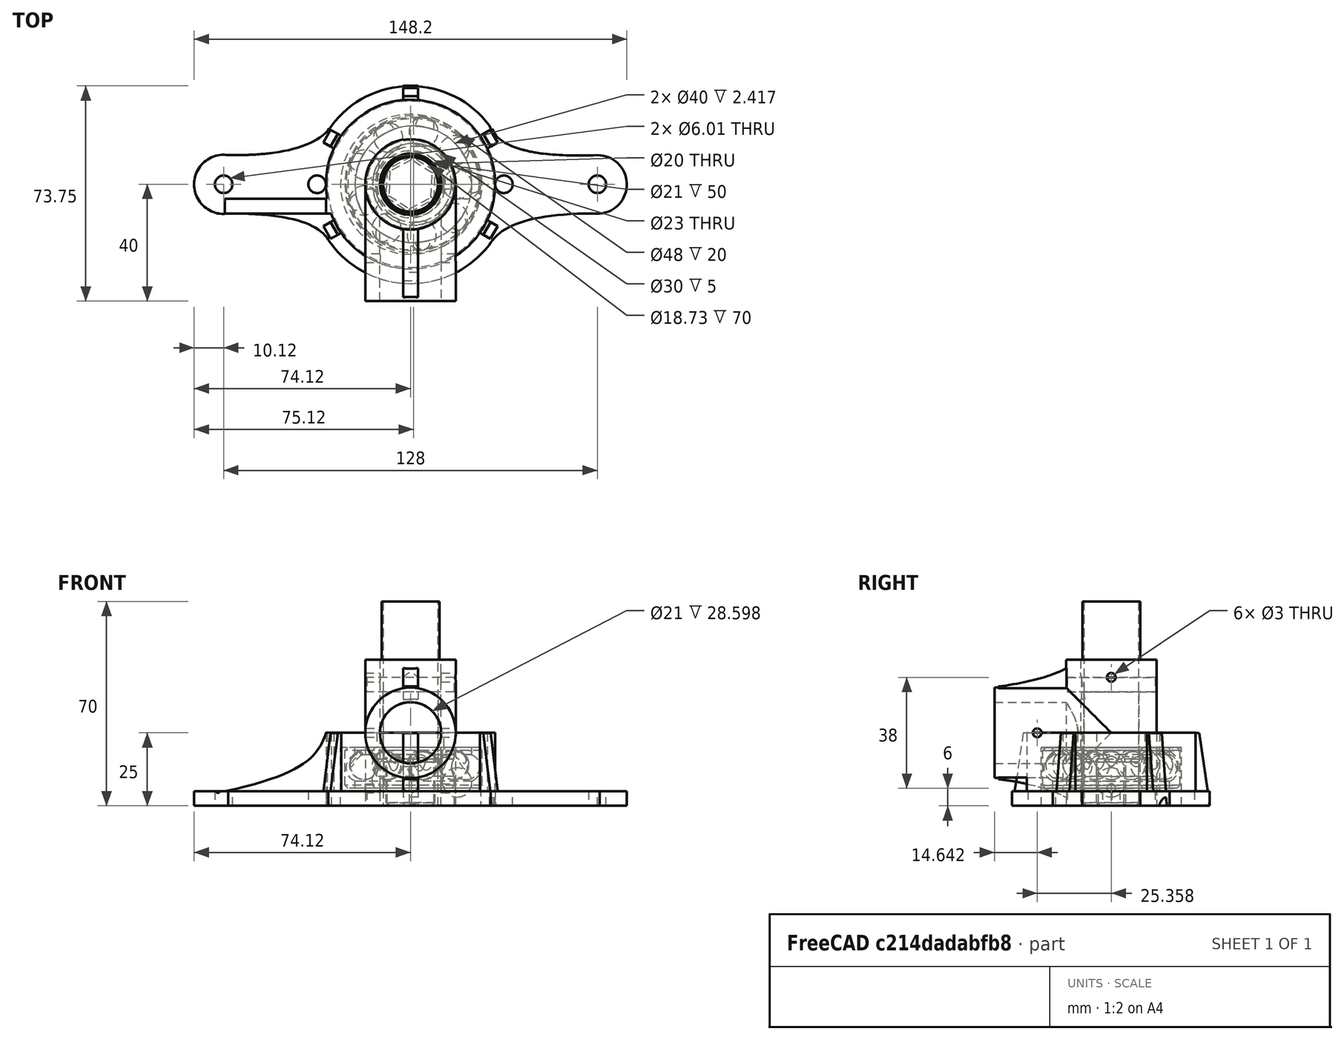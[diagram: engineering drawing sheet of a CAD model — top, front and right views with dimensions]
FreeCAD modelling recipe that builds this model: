
FCSTD DOCUMENT  (FreeCAD 1.0R39109 (Git))
Label: dressingAutomatique
License: All rights reserved
LicenseURL: http://en.wikipedia.org/wiki/All_rights_reserved
objects: Sketcher::SketchObject×16, PartDesign::Pad×10, PartDesign::Pocket×7, App::Link×6, PartDesign::Body×6, App::FeaturePython×5, Part::Chamfer×5, Part::FeaturePython×4, TechDraw::DrawViewDimension×4, TechDraw::DrawProjGroupItem×3, PartDesign::PolarPattern×2, Part::Cut×2, Assembly::JointGroup×1, PartDesign::Chamfer×1, PartDesign::LinearPattern×1, Part::Sphere×1, Part::Torus×1, PartDesign::FeatureBase×1, PartDesign::MultiTransform×1, TechDraw::DrawSVGTemplate×1, +8 more types
note: 121 computed .brp shape members not serialized (recipe doc carries the construction recipe); baked Part::Feature solids carry a one-line shape summary decoded from their .brp

FEATURE [Sketcher::SketchObject] Sketch  label="roulement"
  ArcFitTolerance = 1e-06
  AttachmentSupport = -> [XY_Plane]
  FullyConstrained = true
  MakeInternals = false
  MapMode = 5
  sketch-geometry (2):
    g0: Circle CenterX=0 CenterY=0 CenterZ=0 NormalX=0 NormalY=0 NormalZ=1 AngleXU=0 Radius=11.5
    g1: Circle CenterX=0 CenterY=0 CenterZ=0 NormalX=0 NormalY=0 NormalZ=1 AngleXU=0 Radius=29
  constraints (4):
    c: Coincident(g0,g-1)
    c: Diameter(g0) = 23
    c: Coincident(g1,g0)
    c: Diameter(g1) = 58
FEATURE [Sketcher::SketchObject] Sketch001  label="platine"
  ArcFitTolerance = 1e-06
  AttachmentSupport = -> [XY_Plane]
  FullyConstrained = false
  MakeInternals = false
  MapMode = 5
  sketch-geometry (42):
    g0: LineSegment [constr] StartX=-64.5 StartY=34 StartZ=0 EndX=-64.5 EndY=-34 EndZ=0
    g1: LineSegment [constr] StartX=-64.5 StartY=-34 StartZ=0 EndX=64.5 EndY=-34 EndZ=0
    g2: LineSegment [constr] StartX=64.5 StartY=-34 StartZ=0 EndX=64.5 EndY=34 EndZ=0
    g3: LineSegment [constr] StartX=64.5 StartY=34 StartZ=0 EndX=-64.5 EndY=34 EndZ=0
    g4: GeomPoint [constr] X=47.479 Y=17.6674 Z=0
    g5: ArcOfCircle CenterX=0 CenterY=0 CenterZ=0 NormalX=0 NormalY=0 NormalZ=1 AngleXU=0 Radius=34 StartAngle=3.73456 EndAngle=5.65431
    g6: Circle [constr] CenterX=-62.443 CenterY=-10 CenterZ=0 NormalX=0 NormalY=0 NormalZ=1 AngleXU=0 Radius=1
    g7: Circle [constr] CenterX=-33.5653 CenterY=-9.84859 CenterZ=0 NormalX=0 NormalY=0 NormalZ=1 AngleXU=0 Radius=1
    g8: Circle [constr] CenterX=-28.1957 CenterY=-19 CenterZ=0 NormalX=0 NormalY=0 NormalZ=1 AngleXU=0 Radius=1
    g9: BSplineCurve PolesCount=3 KnotsCount=2 Degree=2 IsPeriodic=0
    g10: GeomPoint [constr] X=-62.443 Y=-10 Z=0
    g11: GeomPoint [constr] X=-28.1957 Y=-19 Z=0
    g12: LineSegment [constr] StartX=-139.75 StartY=-10 StartZ=0 EndX=108.432 EndY=-10 EndZ=0
    g13: LineSegment [constr] StartX=-56.9057 StartY=-20 StartZ=0 EndX=73.6028 EndY=-20 EndZ=0
    g14: ArcOfCircle CenterX=-64 CenterY=0 CenterZ=0 NormalX=0 NormalY=0 NormalZ=1 AngleXU=0 Radius=10.1205 StartAngle=1.41634 EndAngle=4.86685
    g15: BSplineCurve PolesCount=3 KnotsCount=2 Degree=2 IsPeriodic=0
    g16: Circle [constr] CenterX=-62.443 CenterY=10 CenterZ=0 NormalX=0 NormalY=0 NormalZ=1 AngleXU=0 Radius=1
    g17: Circle [constr] CenterX=-33.9289 CenterY=9.66678 CenterZ=0 NormalX=0 NormalY=0 NormalZ=1 AngleXU=0 Radius=1
    g18: Circle [constr] CenterX=-27.0839 CenterY=20.0395 CenterZ=0 NormalX=0 NormalY=0 NormalZ=1 AngleXU=0 Radius=1
    g19: GeomPoint [constr] X=-62.443 Y=10 Z=0
    g20: GeomPoint [constr] X=-27.0839 Y=20.0395 Z=0
    g21: ArcOfCircle CenterX=0 CenterY=0 CenterZ=0 NormalX=0 NormalY=0 NormalZ=1 AngleXU=0 Radius=33.6915 StartAngle=0.637008 EndAngle=2.50458
    g22: ArcOfCircle CenterX=64.071 CenterY=-0.013204 CenterZ=0 NormalX=0 NormalY=0 NormalZ=1 AngleXU=0 Radius=10.0132 StartAngle=4.78503 EndAngle=7.85398
    g23: BSplineCurve PolesCount=3 KnotsCount=2 Degree=2 IsPeriodic=0
    g24: BSplineCurve PolesCount=3 KnotsCount=2 Degree=2 IsPeriodic=0
    g25: Circle [constr] CenterX=64.071 CenterY=10 CenterZ=0 NormalX=0 NormalY=0 NormalZ=1 AngleXU=0 Radius=1
    g26: Circle [constr] CenterX=31.305 CenterY=8.64637 CenterZ=0 NormalX=0 NormalY=0 NormalZ=1 AngleXU=0 Radius=1
    g27: Circle [constr] CenterX=27.0839 CenterY=20.0395 CenterZ=0 NormalX=0 NormalY=0 NormalZ=1 AngleXU=0 Radius=1
    g28: GeomPoint [constr] X=64.071 Y=10 Z=0
    g29: GeomPoint [constr] X=27.0839 Y=20.0395 Z=0
    g30: Circle [constr] CenterX=64.7978 CenterY=-10 CenterZ=0 NormalX=0 NormalY=0 NormalZ=1 AngleXU=0 Radius=1
    g31: Circle [constr] CenterX=33.9289 CenterY=-9.66678 CenterZ=0 NormalX=0 NormalY=0 NormalZ=1 AngleXU=0 Radius=1
    g32: Circle [constr] CenterX=27.4955 CenterY=-20 CenterZ=0 NormalX=0 NormalY=0 NormalZ=1 AngleXU=0 Radius=1
    g33: GeomPoint [constr] X=64.7978 Y=-10 Z=0
    g34: GeomPoint [constr] X=27.4955 Y=-20 Z=0
    g35: LineSegment [constr] StartX=-146.84 StartY=10 StartZ=0 EndX=88.6661 EndY=10 EndZ=0
    g36: LineSegment [constr] StartX=-56.9057 StartY=20.0395 StartZ=0 EndX=73.6028 EndY=20.0395 EndZ=0
    g37: Circle CenterX=-32 CenterY=0 CenterZ=0 NormalX=0 NormalY=0 NormalZ=1 AngleXU=0 Radius=3.00257
    g38: Circle CenterX=0 CenterY=0 CenterZ=0 NormalX=0 NormalY=0 NormalZ=1 AngleXU=0 Radius=3.00257
    g39: Circle CenterX=32 CenterY=0 CenterZ=0 NormalX=0 NormalY=0 NormalZ=1 AngleXU=0 Radius=3.00257
    g40: Circle CenterX=-64 CenterY=0 CenterZ=0 NormalX=0 NormalY=0 NormalZ=1 AngleXU=0 Radius=3.005
    g41: Circle CenterX=64 CenterY=0 CenterZ=0 NormalX=0 NormalY=0 NormalZ=1 AngleXU=0 Radius=3.00257
  constraints (71):
    c: Coincident(g0,g1)
    c: Coincident(g1,g2)
    c: Coincident(g2,g3)
    c: Coincident(g3,g0)
    c: Vertical(g0)
    c: Horizontal(g1)
    c: DistanceY(g2,g2) = 68
    c: DistanceX(g1,g1) = 129
    c: Symmetric(g2,g1,g-1)
    c: Symmetric(g2,g0,g-2)
    c: Weight(g6) = 1
    c: Equal(g6,g7)
    c: Equal(g6,g8)
    c: InternalAlignment(g6,g9)
    c: InternalAlignment(g7,g9)
    c: InternalAlignment(g8,g9)
    c: InternalAlignment(g10,g9)
    c: InternalAlignment(g11,g9)
    c: Coincident(g8,g5)
    c: Horizontal(g12)
    c: Distance(g12,g-1) = 10
    c: Horizontal(g13)
    c: Tangent(g13,g8)
    c: Distance(g13,g-1) = 20
    c: PointOnObject(g5,g13)
    c: Tangent(g5,g1)
    c: Weight(g16) = 1
    c: Equal(g16,g17)
    c: Equal(g16,g18)
    c: InternalAlignment(g16-g20 -> g15) x5
    c: Coincident(g16,g14)
    c: Coincident(g21,g15)
    c: Coincident(g14,g9)
    c: Weight(g30) = 1
    c: Equal(g30,g31)
    c: Equal(g30,g32)
    c: InternalAlignment(g30-g34 -> g24) x5
    c: Weight(g25) = 1
    c: Equal(g25,g26)
    c: Equal(g25,g27)
    c: InternalAlignment(g25-g29 -> g23) x5
    c: Coincident(g25,g22)
    c: Coincident(g22,g24)
    c: Coincident(g24,g5)
    c: Coincident(g23,g21)
    c: PointOnObject(g14,g-1)
    c: PointOnObject(g22,g12)
    c: Horizontal(g35)
    c: Horizontal(g36)
    c: PointOnObject(g21,g36)
    c: PointOnObject(g15,g36)
    c: Diameter(g37) = 6.00515
    c: Diameter(g38) = 6.00515
    c: Diameter(g39) = 6.00515
    c: Coincident(g-1,g5)
    c: Coincident(g-1,g21)
    c: Coincident(g38,g5)
    c: PointOnObject(g37,g-1)
    c: PointOnObject(g39,g-1)
    c: DistanceX(g37,g5) = 32
    c: DistanceX(g5,g39) = 32
    c: PointOnObject(g23,g35)
    c: Diameter(g40) = 6.01
    c: DistanceX(g40,g37) = 32
    c: PointOnObject(g15,g35)
    c: PointOnObject(g9,g12)
    c: Diameter(g41) = 6.00515
    c: PointOnObject(g41,g-1)
    c: DistanceX(g39,g41) = 32
    c: Coincident(g14,g40)
    c: Distance(g35,g-1) = 10
FEATURE [Sketcher::SketchObject] Sketch003  label="renfprt"
  ArcFitTolerance = 1e-06
  AttachmentOffset = pos=(30,0,0) rot=(0,0,1;0rad)
  AttachmentSupport = -> [YZ_Plane]
  FullyConstrained = false
  MakeInternals = false
  MapMode = 5
  Placement = pos=(0,30,0) rot=(0.57735,0.57735,0.57735;2.0944rad)
  sketch-geometry (4):
    g0: LineSegment StartX=-2.07385 StartY=24.959 StartZ=0 EndX=-2.07385 EndY=0 EndZ=0
    g1: LineSegment StartX=-2.07385 StartY=0 StartZ=0 EndX=3.74646 EndY=0 EndZ=0
    g2: LineSegment StartX=-2.07385 StartY=24.959 StartZ=0 EndX=0.193659 EndY=24.959 EndZ=0
    g3: LineSegment StartX=0.193659 StartY=24.959 StartZ=0 EndX=3.74646 EndY=0 EndZ=0
  constraints (8):
    c: Coincident(g0,g1)
    c: Vertical(g0)
    c: Horizontal(g1)
    c: PointOnObject(g1,g-1)
    c: Coincident(g2,g0)
    c: Coincident(g3,g2)
    c: Coincident(g3,g1)
    c: Horizontal(g2)
FEATURE [Sketcher::SketchObject] Sketch004  label="axe"
  ArcFitTolerance = 1e-06
  AttachmentSupport = -> [XY_Plane001]
  FullyConstrained = true
  MakeInternals = false
  MapMode = 5
  sketch-geometry (2):
    g0: Circle CenterX=0 CenterY=0 CenterZ=0 NormalX=0 NormalY=0 NormalZ=1 AngleXU=0 Radius=15
    g1: Circle CenterX=0 CenterY=0 CenterZ=0 NormalX=0 NormalY=0 NormalZ=1 AngleXU=0 Radius=9.5
  constraints (4):
    c: Coincident(g0,g-1)
    c: Diameter(g0) = 30
    c: Coincident(g1,g0)
    c: Diameter(g1) = 19
FEATURE [PartDesign::Pad] Pad004  label="bute axe"
  Direction = (0,0,1)
  Length = 44
  Length2 = 10
  Profile = -> Sketch004 [Edge1]
  ReferenceAxis = -> Sketch004 [N_Axis]
  Suppressed = false
  Type = 0
FEATURE [PartDesign::Pocket] Pocket001  label="axe001"
  BaseFeature = -> Pad004
  Direction = (0,0,-1)
  Length = 39
  Length2 = 5
  Profile = -> Sketch004
  ReferenceAxis = -> Sketch004 [N_Axis]
  Reversed = true
  Suppressed = false
  Type = 0
FEATURE [Sketcher::SketchObject] Sketch005  label="hexa"
  ArcFitTolerance = 1e-06
  AttachmentSupport = -> [XY_Plane001]
  ExternalGeometry = -> [Sketch004]
  FullyConstrained = false
  MakeInternals = false
  MapMode = 5
  sketch-geometry (8):
    g0: LineSegment StartX=8.03876 StartY=-5.06244 StartZ=0 EndX=8.40359 EndY=4.43055 EndZ=0
    g1: LineSegment StartX=8.40359 StartY=4.43055 StartZ=0 EndX=0.364825 EndY=9.49299 EndZ=0
    g2: LineSegment StartX=0.364825 StartY=9.49299 StartZ=0 EndX=-8.03876 EndY=5.06244 EndZ=0
    g3: LineSegment StartX=-8.03876 StartY=5.06244 StartZ=0 EndX=-8.40359 EndY=-4.43055 EndZ=0
    g4: LineSegment StartX=-8.40359 StartY=-4.43055 StartZ=0 EndX=-0.364825 EndY=-9.49299 EndZ=0
    g5: LineSegment StartX=-0.364825 StartY=-9.49299 StartZ=0 EndX=8.03876 EndY=-5.06244 EndZ=0
    g6: Circle [constr] CenterX=0 CenterY=0 CenterZ=0 NormalX=0 NormalY=0 NormalZ=1 AngleXU=0 Radius=9.5
    g7: Circle CenterX=0 CenterY=0 CenterZ=0 NormalX=0 NormalY=0 NormalZ=1 AngleXU=0 Radius=12.1402
  constraints (16):
    c: Coincident(g0,g1)
    c: Coincident(g1,g2)
    c: Coincident(g2,g3)
    c: Coincident(g3,g4)
    c: Coincident(g4,g5)
    c: Coincident(g5,g0)
    c: Equal(g0, g1-g5) x5
    c: PointOnObject(g0,g6)
    c: PointOnObject(g1,g6)
    c: PointOnObject(g2,g6)
    c: PointOnObject(g3,g6)
    c: PointOnObject(g4,g6)
    c: PointOnObject(g5,g6)
    c: Coincident(g6,g-1)
    c: PointOnObject(g5,g-3)
    c: Coincident(g7,g6)
FEATURE [PartDesign::Pocket] Pocket002
  BaseFeature = -> Pocket001
  Direction = (0,0,-1)
  Length = 15
  Length2 = 5
  Profile = -> Sketch005
  ReferenceAxis = -> Sketch005 [N_Axis]
  Reversed = true
  Suppressed = false
  Type = 0
FEATURE [App::Link] Support_mur  label="Support mur001"
  LinkedObject = -> Body
FEATURE [App::FeaturePython] GroundedJoint  # Assembly grounded joint (typed FeaturePython)
  ObjectToGround = -> Support_mur
FEATURE [Assembly::JointGroup] Joints
  Group = -> [GroundedJoint]
FEATURE [App::Link] Axe  label="Axe001"
  LinkPlacement = pos=(-8.9e-15,-2.04251e-06,32) rot=(1,0,0;3.14159rad)
  LinkedObject = -> Body001
  Placement = pos=(-8.9e-15,-2.04251e-06,32) rot=(1,0,0;3.14159rad)
FEATURE [PartDesign::Chamfer] Chamfer
  Angle = 45
  Base = -> Pocket002 [Edge25,Edge23,Edge21,Edge30,Face17,Edge27]
  BaseFeature = -> Pocket002
  ChamferType = 0
  FlipDirection = false
  Size = 1
  Size2 = 1
  SupportTransform = false
  Suppressed = false
  UseAllEdges = false
FEATURE [PartDesign::Body] Body001  label="Axe"
  AllowCompound = false
  Group = -> [Sketch004,Pad004,Pocket001,Sketch005,Pocket002,Chamfer]
  Origin = -> Origin001
  Tip = -> Chamfer
FEATURE [Sketcher::SketchObject] Sketch006
  ArcFitTolerance = 1e-06
  AttachmentOffset = pos=(0,0,5) rot=(0,0,1;0rad)
  AttachmentSupport = -> [XZ_Plane]
  FullyConstrained = false
  MakeInternals = false
  MapMode = 5
  Placement = pos=(0,-5,1.1e-15) rot=(1,0,0;1.5708rad)
  sketch-geometry (11):
    g0: LineSegment StartX=-66.3753 StartY=4.44189 StartZ=0 EndX=-26.6331 EndY=4.44189 EndZ=0
    g1: LineSegment StartX=-26.6331 StartY=4.44189 StartZ=0 EndX=-26.6331 EndY=25 EndZ=0
    g2: GeomPoint [constr] X=-28.9519 Y=25 Z=0
    g3: GeomPoint [constr] X=-38.0241 Y=13.5983 Z=0
    g4: GeomPoint [constr] X=-66.3753 Y=4.44189 Z=0
    g5: BSplineCurve PolesCount=4 KnotsCount=2 Degree=3 IsPeriodic=0
    g6-g9: Circle [constr] x4 (B-spline internal-alignment scaffolding for g5; pole/knot coordinates omitted)
    g10: LineSegment StartX=-26.6331 StartY=25 StartZ=0 EndX=-28.9519 EndY=25 EndZ=0
  constraints (19):
    c: Vertical(g1)
    c: InternalAlignment(g2,g5)
    c: PointOnObject(g3,g5)
    c: InternalAlignment(g4,g5)
    c: InternalAlignment(g6,g5)
    c: Weight(g6) = 1
    c: InternalAlignment(g7,g5)
    c: Equal(g7,g6)
    c: InternalAlignment(g8,g5)
    c: Equal(g8,g6)
    c: InternalAlignment(g9,g5)
    c: Equal(g9,g6)
    c: Coincident(g1,g0)
    c: Coincident(g5,g0)
    c: Horizontal(g0)
    c: PointOnObject(g1,g-3)
    c: Coincident(g10,g1)
    c: PointOnObject(g10,g-3)
    c: Coincident(g5,g10)
FEATURE [PartDesign::LinearPattern] LinearPattern
  Direction = -> Y_Axis
  Length = 15
  Mode = 0
  Occurrences = 2
  Offset = 15
  Suppressed = false
  TransformMode = 0
FEATURE [PartDesign::PolarPattern] PolarPattern002
  Angle = 360
  Axis = -> Z_Axis
  Mode = 0
  Occurrences = 2
  Offset = 120
  Suppressed = false
  TransformMode = 0
FEATURE [Part::Sphere] Sphere
  Angle1 = -90
  Angle2 = 90
  Angle3 = 360
  AttacherType = Attacher::AttachEngine3D
  Placement = pos=(16,0,8) rot=(0,0,1;0rad)
  Radius = 5
FEATURE [Part::FeaturePython] Tube  # WARN: FeaturePython — macro-defined, semantics opaque (R4)
  AttacherType = Attacher::AttachEngine3D
  Height = 14
  InnerRadius = 10
  OuterRadius = 14
FEATURE [Part::Torus] Torus
  Angle1 = -180
  Angle2 = 180
  Angle3 = 360
  AttacherType = Attacher::AttachEngine3D
  Placement = pos=(0,0,7) rot=(0,0,1;0rad)
  Radius1 = 18
  Radius2 = 5
FEATURE [Part::FeaturePython] Tube001  # WARN: FeaturePython — macro-defined, semantics opaque (R4)
  AttacherType = Attacher::AttachEngine3D
  Height = 14
  InnerRadius = 20
  OuterRadius = 23.5
FEATURE [Part::Cut] Cut002
  Base = -> Tube001
  Tool = -> Torus
FEATURE [Part::Cut] Cut
  Base = -> Tube
  Tool = -> Torus
FEATURE [Part::Chamfer] Chamfer001
  Base = -> Cut002
  EdgeLinks = -> Cut002 [Edge1]
  Edges = 1 edges r=1: [Edge1]
FEATURE [Part::Chamfer] Chamfer002
  Base = -> Chamfer001
  EdgeLinks = -> Chamfer001 [Edge3]
  Edges = 1 edges r=1: [Edge3]
FEATURE [Part::Chamfer] Chamfer003
  Base = -> Cut
  EdgeLinks = -> Cut [Edge3]
  Edges = 1 edges r=1: [Edge3]
FEATURE [Part::Chamfer] Chamfer004
  Base = -> Chamfer003
  EdgeLinks = -> Chamfer003 [Edge8]
  Edges = 1 edges r=1: [Edge8]
FEATURE [Part::Chamfer] Chamfer005
  Base = -> Chamfer004
  EdgeLinks = -> Chamfer004 [Edge8,Edge11]
  Edges = 2 edges r=1: [Edge8,Edge11]
FEATURE [Part::FeaturePython] Array  # Draft array (typed FeaturePython)
  AlwaysSyncPlacement = false
  Angle = 360
  ArrayType = 1
  Axis = (0,0,1)
  Base = -> Sphere
  Center = (-1.96,0.32,0.26)
  Count = 9
  ExpandArray = false
  Fuse = false
  IntervalAxis = (0,0,0)
  IntervalX = (50,0,0)
  IntervalY = (0,50,0)
  IntervalZ = (0,0,50)
  NumberCircles = 3
  NumberPolar = 9
  NumberX = 2
  NumberY = 2
  NumberZ = 1
  Placement = pos=(2,-2.38419e-07,0) rot=(0,0,1;0rad)
  PlacementList = 9 placements: [(16,0,8),(12.0039,11.6193,8),(1.47386,17.9516,8),(-10.6629,16.0338,8),(-18.7274,6.76338,8),(-18.9463,-5.52198,8),(-11.2171,-15.0738,8),(0.843583,-17.4227,8),(11.5925,-11.4696,8)]
  RadialDistance = 50
  ScaleList = (9) [(1,1,1),(1,1,1),(1,1,1),(1,1,1),(1,1,1),(1,1,1),(1,1,1),(1,1,1),(1,1,1)]
  Symmetry = 1
  TangentialDistance = 25
FEATURE [Part::FeaturePython] Connect  # WARN: FeaturePython — macro-defined, semantics opaque (R4)
  Objects = -> [Chamfer002,Chamfer005,Array]
  Tolerance = 0
FEATURE [PartDesign::FeatureBase] BaseFeature
  BaseFeature = -> Connect
  Suppressed = false
FEATURE [PartDesign::Body] Body002  label="Roulement"
  AllowCompound = false
  BaseFeature = -> Connect
  Group = -> [BaseFeature]
  Origin = -> Origin003
  Placement = pos=(0.999972,4.76837e-06,6.00003) rot=(0,0,1;0rad)
  Tip = -> BaseFeature
FEATURE [Sketcher::SketchObject] Sketch007  label="roulement insert"
  ArcFitTolerance = 1e-06
  AttachmentSupport = -> [XY_Plane]
  FullyConstrained = true
  MakeInternals = false
  MapMode = 5
  sketch-geometry (1):
    g0: Circle CenterX=0 CenterY=0 CenterZ=0 NormalX=0 NormalY=0 NormalZ=1 AngleXU=0 Radius=24
  constraints (2):
    c: Coincident(g0,g-1)
    c: Radius(g0) = 24
FEATURE [PartDesign::Pad] Pad
  Direction = (0,0,1)
  Length = 25
  Length2 = 10
  Profile = -> Sketch
  ReferenceAxis = -> Sketch [N_Axis]
  Suppressed = false
  Type = 0
FEATURE [PartDesign::Pad] Pad001
  BaseFeature = -> Pad
  Direction = (0,0,1)
  Length = 5
  Length2 = 10
  Profile = -> Sketch001
  ReferenceAxis = -> Sketch001 [N_Axis]
  Suppressed = false
  Type = 0
FEATURE [PartDesign::Pocket] Pocket
  BaseFeature = -> Pad001
  Direction = (0,0,-1)
  Length = 20
  Length2 = 10
  Profile = -> Sketch007
  ReferenceAxis = -> Sketch007 [N_Axis]
  Reversed = true
  Suppressed = false
  Type = 4
FEATURE [PartDesign::Pad] Pad003  label="renfort roulement"
  BaseFeature = -> Pocket
  Direction = (1,0,0)
  Length = 2.5
  Length2 = 2.5
  Profile = -> Sketch003
  ReferenceAxis = -> Sketch003 [N_Axis]
  Suppressed = false
  Type = 4
FEATURE [PartDesign::PolarPattern] PolarPattern
  Angle = 360
  Axis = -> Z_Axis
  BaseFeature = -> Pad003
  Mode = 0
  Occurrences = 6
  Offset = 120
  Originals = -> [Pad003]
  Suppressed = false
  TransformMode = 0
FEATURE [PartDesign::Pad] Pad005  label="renfort platine"
  BaseFeature = -> PolarPattern
  Direction = (0,-1,2e-16)
  Length = 5
  Length2 = 15
  Profile = -> Sketch006
  ReferenceAxis = -> Sketch006 [N_Axis]
  Suppressed = false
  Type = 0
FEATURE [PartDesign::MultiTransform] MultiTransform
  BaseFeature = -> Pad005
  Originals = -> [Pad005]
  Suppressed = false
  TransformMode = 0
  Transformations = -> [LinearPattern,PolarPattern002]
FEATURE [Sketcher::SketchObject] Sketch008
  ArcFitTolerance = 1e-06
  AttachmentOffset = pos=(0,0,5) rot=(0,0,1;0rad)
  AttachmentSupport = -> [XY_Plane]
  ExternalGeometry = -> [Sketch001]
  FullyConstrained = true
  MakeInternals = false
  MapMode = 5
  Placement = pos=(0,0,5) rot=(0,0,1;0rad)
  sketch-geometry (2):
    g0: Circle CenterX=-32 CenterY=0 CenterZ=0 NormalX=0 NormalY=0 NormalZ=1 AngleXU=0 Radius=4.5
    g1: Circle CenterX=32 CenterY=0 CenterZ=0 NormalX=0 NormalY=0 NormalZ=1 AngleXU=0 Radius=4.5
  constraints (4):
    c: Coincident(g0,g-3)
    c: Coincident(g1,g-4)
    c: Diameter(g0) = 9
    c: Diameter(g1) = 9
FEATURE [PartDesign::Pocket] Pocket003
  BaseFeature = -> MultiTransform
  Direction = (0,0,-1)
  Length = 28
  Length2 = 5
  Profile = -> Sketch008
  ReferenceAxis = -> Sketch008 [N_Axis]
  Reversed = true
  Suppressed = false
  Type = 0
FEATURE [PartDesign::Body] Body  label="Support mur"
  AllowCompound = false
  Group = -> [Pad,Pad001,Sketch,Pocket,Sketch001,Sketch003,Pad003,PolarPattern,Sketch006,Pad005,PolarPattern002,Sketch007,Sketch008,MultiTransform,Pocket003,LinearPattern]
  Origin = -> Origin
  Tip = -> Pad005
FEATURE [TechDraw::DrawSVGTemplate] Template
  EditableTexts = approval_person=B. Hecate; creator=A. Nemesis; date_of_issue=26/01/2025; document_status=In preparation; document_type=Assembly Drawing; drawing_number=DN; general_tolerances=ISO 2768-m; language_code=EN; part_material=Stainless steel Mat.No. 1.4301; responsible_department=RD; revision_index=AAA; sheet_number=1 / 1; sheet_scale=1 : 1; supplementary_title_1=ST1; supplementary_title_2=ST2; title=dressingAutomatique
  Height = 594
  Orientation = 1
  Template = D:/Program Files/FreeCAD 1.0/data/Mod/TechDraw/Templates/A1_Landscape_ISO5457_advanced.svg
  Width = 841
FEATURE [TechDraw::DrawProjGroupItem] View  label="Front"
  CoarseView = false
  Direction = (0,-1,0)
  Focus = 100
  HardHidden = false
  IsoCount = 0
  IsoHidden = false
  IsoVisible = false
  LockPosition = true
  Perspective = false
  Rotation = 0
  RotationVector = (1,0,0)
  ScaleType = 2
  ScrubCount = 1
  SeamHidden = false
  SeamVisible = false
  SmoothHidden = false
  SmoothVisible = true
  Source = -> [Pocket003]
  Type = 0
  X = 0
  XDirection = (1,0,0)
  Y = 0
FEATURE [TechDraw::DrawProjGroupItem] ProjItem  label="Bottom"
  CoarseView = false
  Direction = (0,0,-1)
  Focus = 100
  HardHidden = false
  IsoCount = 0
  IsoHidden = false
  IsoVisible = false
  LockPosition = false
  Perspective = false
  Rotation = 0
  RotationVector = (1,0,0)
  ScaleType = 0
  ScrubCount = 1
  SeamHidden = false
  SeamVisible = false
  SmoothHidden = false
  SmoothVisible = true
  Source = -> [Pocket003]
  Type = 5
  X = 0
  XDirection = (1,0,0)
  Y = 61.3732
FEATURE [TechDraw::DrawProjGroupItem] ProjItem002  label="Top"
  CoarseView = false
  Direction = (0,0,1)
  Focus = 100
  HardHidden = false
  IsoCount = 0
  IsoHidden = false
  IsoVisible = false
  LockPosition = false
  Perspective = false
  Rotation = 0
  RotationVector = (1,0,0)
  ScaleType = 0
  ScrubCount = 1
  SeamHidden = false
  SeamVisible = false
  SmoothHidden = false
  SmoothVisible = true
  Source = -> [Pocket003]
  Type = 4
  X = 0
  XDirection = (1,0,0)
  Y = -61.3732
FEATURE [TechDraw::DrawProjGroup] ProjGroup
  Anchor = -> View
  AutoDistribute = true
  LockPosition = false
  ProjectionType = 0
  Rotation = 0
  ScaleType = 0
  Source = -> [Pocket003]
  Views = -> [View,ProjItem,ProjItem002]
  X = 225.734
  Y = 323.245
  spacingX = 15
  spacingY = 15
FEATURE [TechDraw::DrawViewBalloon] Balloon
  BubbleShape = 0
  EndType = 0
  EndTypeScale = 1
  KinkLength = 5
  LockPosition = false
  OriginX = 5.51711
  OriginY = 71.03
  Rotation = 0
  ScaleType = 0
  ShapeScale = 1
  SourceView = -> View
  Text = 1
  TextWrapLen = -1
  X = 25.5171
  Y = 91.03
FEATURE [TechDraw::DrawViewDimension] Dimension
  AngleOverride = false
  Arbitrary = false
  ArbitraryTolerances = false
  BoxCorners = (2) [(-74.1024,-33.8732,-1e-07),(74.1024,33.8732,1e-07)]
  EqualTolerance = true
  ExtensionAngle = 0
  FormatSpec = ⌀%.2w
  FormatSpecOverTolerance = %+.2w
  FormatSpecUnderTolerance = %+.2w
  Inverted = false
  LineAngle = 0
  LockPosition = false
  MeasureType = 1
  OverTolerance = 0
  References2D = -> [ProjItem]
  Rotation = 0
  ScaleType = 0
  TheoreticalExact = false
  Type = 5
  UnderTolerance = 0
  X = 67.3072
  Y = 46.6106
FEATURE [TechDraw::DrawViewSection] SectionView  label="Section  - "
  BaseView = -> View
  CoarseView = false
  CutSurfaceDisplay = 2
  Direction = (-1,0,-1e-16)
  FileGeomPattern = <path>\data\Mod/TechDraw/PAT/FCPAT.pat
  FileHatchPattern = <path>\data\Mod/TechDraw/Patterns/simple.svg
  Focus = 100
  FuseBeforeCut = false
  HardHidden = false
  HatchOffset = (0,0,0)
  HatchRotation = 0
  HatchScale = 1
  IsoCount = 0
  IsoHidden = false
  IsoVisible = false
  LockPosition = false
  NameGeomPattern = Diamond
  Perspective = false
  Rotation = -90
  ScaleType = 0
  ScrubCount = 1
  SeamHidden = false
  SeamVisible = false
  SectionDirection = 4
  SectionLineStretch = 1
  SectionNormal = (-1,0,-1e-16)
  SectionOrigin = (-0.018,-0.13,12.5)
  SmoothHidden = false
  SmoothVisible = true
  Source = -> [Pocket003]
  TrimAfterCut = false
  UsePreviousCut = false
  X = 361.548
  XDirection = (1e-16,0,-1)
  Y = 500.685
FEATURE [TechDraw::DrawViewImage] ActiveView
  Height = 102.4
  ImageFile = <userpath>/AppData/Local/cache/FreeCAD/Cache/FreeCAD_Doc_1c473428-2d88-4942-b3bc-02458ee26885_3d8759_5548/PagC9F4.tmp.png
  LockPosition = false
  Rotation = 0
  ScaleType = 2
  Width = 128
  X = 634.849
  Y = 481.794
FEATURE [TechDraw::DrawViewDimension] Dimension001
  AngleOverride = false
  Arbitrary = false
  ArbitraryTolerances = false
  BoxCorners = (2) [(-74.1024,-33.8732,-1e-07),(74.1024,33.8732,1e-07)]
  EqualTolerance = true
  ExtensionAngle = 0
  FormatSpec = ⌀%.2w
  FormatSpecOverTolerance = %+.2w
  FormatSpecUnderTolerance = %+.2w
  Inverted = false
  LineAngle = 0
  LockPosition = false
  MeasureType = 1
  OverTolerance = 0
  References2D = -> [ProjItem002]
  Rotation = 0
  ScaleType = 0
  TheoreticalExact = false
  Type = 5
  UnderTolerance = 0
  X = -49.8224
  Y = 44.2381
FEATURE [TechDraw::DrawViewDimension] Dimension002
  AngleOverride = false
  Arbitrary = false
  ArbitraryTolerances = false
  BoxCorners = (2) [(-74.1024,-33.8732,-1e-07),(74.1024,33.8732,1e-07)]
  EqualTolerance = true
  ExtensionAngle = 0
  FormatSpec = R%.2w
  FormatSpecOverTolerance = %+.2w
  FormatSpecUnderTolerance = %+.2w
  Inverted = false
  LineAngle = 0
  LockPosition = false
  MeasureType = 1
  OverTolerance = 0
  References2D = -> [ProjItem002]
  Rotation = 0
  ScaleType = 0
  TheoreticalExact = false
  Type = 4
  UnderTolerance = 0
  X = 38.0612
  Y = 49.8635
FEATURE [TechDraw::DrawViewDimension] Dimension003
  AngleOverride = false
  Arbitrary = false
  ArbitraryTolerances = false
  BoxCorners = (2) [(-33.8732,-12.5,-1e-07),(33.8732,12.5,1e-07)]
  EqualTolerance = true
  ExtensionAngle = 0
  FormatSpec = %.2w
  FormatSpecOverTolerance = %+.2w
  FormatSpecUnderTolerance = %+.2w
  Inverted = false
  LineAngle = 0
  LockPosition = false
  MeasureType = 1
  OverTolerance = 0
  References2D = -> [SectionView]
  Rotation = 0
  ScaleType = 0
  TheoreticalExact = false
  Type = 1
  UnderTolerance = 0
  X = -0.12677
  Y = -42.2028
FEATURE [TechDraw::DrawPage] Page
  KeepUpdated = true
  NextBalloonIndex = 2
  ProjectionType = 0
  Template = -> Template
  Views = -> [ProjGroup,Balloon,Dimension,SectionView,ActiveView,Dimension001,Dimension002,Dimension003]
FEATURE [Sketcher::SketchObject] Sketch009
  ArcFitTolerance = 1e-06
  AttachmentSupport = -> [XY_Plane004]
  FullyConstrained = true
  MakeInternals = false
  MapMode = 5
  sketch-geometry (2):
    g0: Circle CenterX=0 CenterY=0 CenterZ=0 NormalX=0 NormalY=0 NormalZ=1 AngleXU=0 Radius=28.5
    g1: Circle CenterX=0 CenterY=0 CenterZ=0 NormalX=0 NormalY=0 NormalZ=1 AngleXU=0 Radius=15
  constraints (4):
    c: Coincident(g0,g-1)
    c: Coincident(g1,g0)
    c: Diameter(g0) = 57
    c: Diameter(g1) = 30
FEATURE [PartDesign::Pad] Pad006
  Direction = (0,0,1)
  Length = 5
  Length2 = 10
  Profile = -> Sketch009
  ReferenceAxis = -> Sketch009 [N_Axis]
  Suppressed = false
  Type = 0
FEATURE [Sketcher::SketchObject] Sketch010
  ArcFitTolerance = 1e-06
  AttachmentSupport = -> [XY_Plane004]
  FullyConstrained = true
  MakeInternals = false
  MapMode = 5
  sketch-geometry (1):
    g0: Circle CenterX=0 CenterY=0 CenterZ=0 NormalX=0 NormalY=0 NormalZ=1 AngleXU=0 Radius=23.5
  constraints (2):
    c: Coincident(g0,g-1)
    c: Diameter(g0) = 47
FEATURE [PartDesign::Pocket] Pocket004
  BaseFeature = -> Pad006
  Direction = (0,0,-1)
  Length = 2
  Length2 = 5
  Profile = -> Sketch010
  ReferenceAxis = -> Sketch010 [N_Axis]
  Suppressed = false
  Type = 0
FEATURE [PartDesign::Body] Body003  label="Bouchon"
  AllowCompound = false
  Group = -> [Sketch009,Pad006,Sketch010,Pocket004]
  Origin = -> Origin004
  Tip = -> Pocket004
FEATURE [App::Link] Bouchon  label="Bouchon001"
  LinkPlacement = pos=(-2.38419e-06,-1.06904e-06,-58.0001) rot=(1,0,0;3.14159rad)
  LinkedObject = -> Body003
  Placement = pos=(-2.38419e-06,-1.06904e-06,-58.0001) rot=(1,0,0;3.14159rad)
FEATURE [App::FeaturePython] Move  # WARN: FeaturePython — macro-defined, semantics opaque (R4)
  MoveType = 1
  MovementTransform = pos=(0,1e-05,-54.0002) rot=(0,0,1;0rad)
  References = -> Assembly [Support_mur.,Connect.,Body002.,Bouchon.]
FEATURE [App::FeaturePython] Move001  # WARN: FeaturePython — macro-defined, semantics opaque (R4)
  MoveType = 0
  MovementTransform = pos=(0,0,-15) rot=(0,0,1;0rad)
  References = -> Assembly [Body002.]
FEATURE [App::FeaturePython] Move002  # WARN: FeaturePython — macro-defined, semantics opaque (R4)
  MoveType = 0
  MovementTransform = pos=(0,0,13) rot=(0,0,1;0rad)
  References = -> Assembly [Support_mur.]
FEATURE [App::FeaturePython] Exploded_View  # WARN: FeaturePython — macro-defined, semantics opaque (R4)
  Moves = -> [Move,Move001,Move002]
FEATURE [Assembly::ViewGroup] Exploded_Views
  Group = -> [Exploded_View]
FEATURE [Sketcher::SketchObject] Sketch011
  ArcFitTolerance = 1e-06
  AttachmentSupport = -> [XY_Plane005]
  FullyConstrained = false
  MakeInternals = false
  MapMode = 5
  sketch-geometry (1):
    g0: Circle CenterX=0 CenterY=0 CenterZ=0 NormalX=0 NormalY=0 NormalZ=1 AngleXU=0 Radius=15.5
  constraints (1):
    c: Diameter(g0) = 31
FEATURE [Sketcher::SketchObject] Sketch012
  ArcFitTolerance = 1e-06
  AttachmentSupport = -> [XZ_Plane005]
  FullyConstrained = false
  MakeInternals = false
  MapMode = 5
  Placement = pos=(0,0,0) rot=(1,0,0;1.5708rad)
  sketch-geometry (2):
    g0: Circle CenterX=0 CenterY=25 CenterZ=0 NormalX=0 NormalY=0 NormalZ=1 AngleXU=0 Radius=15.5
    g1: Circle CenterX=0 CenterY=25 CenterZ=0 NormalX=0 NormalY=0 NormalZ=1 AngleXU=0 Radius=10.5
  constraints (4):
    c: Diameter(g0) = 31
    c: DistanceY(g-1,g0) = 25
    c: Coincident(g1,g0)
    c: Diameter(g1) = 21
FEATURE [PartDesign::Pad] Pad008
  Direction = (0,-1,2e-16)
  Length = 40
  Length2 = 10
  Placement = pos=(0,0,0) rot=(1,0,0;1.5708rad)
  Profile = -> Sketch012
  ReferenceAxis = -> Sketch012 [N_Axis]
  Suppressed = false
  Type = 0
FEATURE [PartDesign::Pad] Pad007
  BaseFeature = -> Pad008
  Direction = (0,0,1)
  Length = 50
  Length2 = 10
  Placement = pos=(0,0,0) rot=(1,0,0;1.5708rad)
  Profile = -> Sketch011
  ReferenceAxis = -> Sketch011 [N_Axis]
  Suppressed = false
  Type = 0
FEATURE [Sketcher::SketchObject] Sketch013
  ArcFitTolerance = 1e-06
  AttachmentSupport = -> [XY_Plane005]
  FullyConstrained = true
  MakeInternals = false
  MapMode = 5
  sketch-geometry (1):
    g0: Circle CenterX=0 CenterY=0 CenterZ=0 NormalX=0 NormalY=0 NormalZ=1 AngleXU=0 Radius=10.5
  constraints (2):
    c: Coincident(g0,g-1)
    c: Diameter(g0) = 21
FEATURE [PartDesign::Pocket] Pocket005
  BaseFeature = -> Pad007
  Direction = (0,0,-1)
  Length = 5
  Length2 = 5
  Placement = pos=(0,0,0) rot=(1,0,0;1.5708rad)
  Profile = -> Sketch013
  ReferenceAxis = -> Sketch013 [N_Axis]
  Reversed = true
  Suppressed = false
  Type = 1
FEATURE [Sketcher::SketchObject] Sketch014
  ArcFitTolerance = 1e-06
  AttachmentOffset = pos=(0,1.5,-2.5) rot=(0,0,1;0rad)
  AttachmentSupport = -> [YZ_Plane005]
  ExternalGeometry = -> [Sketch012]
  FullyConstrained = false
  MakeInternals = false
  MapMode = 5
  Placement = pos=(-2.5,0,1.5) rot=(0.57735,0.57735,0.57735;2.0944rad)
  sketch-geometry (10):
    g0: Circle [constr] CenterX=-38.6494 CenterY=39.3664 CenterZ=0 NormalX=0 NormalY=0 NormalZ=1 AngleXU=0 Radius=1
    g1: Circle [constr] CenterX=-19.1662 CenterY=41.8877 CenterZ=0 NormalX=0 NormalY=0 NormalZ=1 AngleXU=0 Radius=1
    g2: Circle [constr] CenterX=-11.1428 CenterY=48.3038 CenterZ=0 NormalX=0 NormalY=0 NormalZ=1 AngleXU=0 Radius=1
    g3: BSplineCurve PolesCount=3 KnotsCount=2 Degree=2 IsPeriodic=0
    g4: GeomPoint [constr] X=-38.6494 Y=39.3664 Z=0
    g5: GeomPoint [constr] X=-11.1428 Y=48.3038 Z=0
    g6: LineSegment StartX=-11.1428 StartY=48.3038 StartZ=0 EndX=-9.08077 EndY=35.0113 EndZ=0
    g7: LineSegment StartX=-9.08077 StartY=35.0113 StartZ=0 EndX=-38.8787 EndY=35.0113 EndZ=0
    g8: LineSegment StartX=-38.8787 StartY=35.0113 StartZ=0 EndX=-38.6494 EndY=39.3664 EndZ=0
    g9: LineSegment [constr] StartX=-43.4272 StartY=23.5 StartZ=0 EndX=46.883 EndY=23.5 EndZ=0
  constraints (14):
    c: Weight(g0) = 1
    c: Equal(g0,g1)
    c: Equal(g0,g2)
    c: InternalAlignment(g0,g3)
    c: InternalAlignment(g1,g3)
    c: InternalAlignment(g2,g3)
    c: InternalAlignment(g4,g3)
    c: InternalAlignment(g5,g3)
    c: Coincident(g6,g3)
    c: Coincident(g7,g6)
    c: Horizontal(g7)
    c: Coincident(g8,g7)
    c: Coincident(g8,g3)
    c: Symmetric(g-3,g-3,g9)
FEATURE [PartDesign::Pad] Pad009
  BaseFeature = -> Pocket005
  Direction = (1,0,0)
  Length = 5
  Length2 = 10
  Placement = pos=(0,0,0) rot=(1,0,0;1.5708rad)
  Profile = -> Sketch014
  ReferenceAxis = -> Sketch014 [N_Axis]
  Suppressed = false
  Type = 0
FEATURE [PartDesign::Mirrored] Mirrored
  BaseFeature = -> Pad009
  MirrorPlane = -> Sketch014 [Axis]
  Originals = -> [Pad009]
  Placement = pos=(0,0,0) rot=(1,0,0;1.5708rad)
  Suppressed = false
  TransformMode = 0
FEATURE [Sketcher::SketchObject] Sketch015
  ArcFitTolerance = 1e-06
  AttachmentSupport = -> [YZ_Plane005]
  FullyConstrained = false
  MakeInternals = false
  MapMode = 5
  Placement = pos=(0,0,0) rot=(0.57735,0.57735,0.57735;2.0944rad)
  sketch-geometry (4):
    g0: Circle CenterX=0 CenterY=6 CenterZ=0 NormalX=0 NormalY=0 NormalZ=1 AngleXU=0 Radius=1.5
    g1: Circle CenterX=0 CenterY=44 CenterZ=0 NormalX=0 NormalY=0 NormalZ=1 AngleXU=0 Radius=1.5
    g2: Circle CenterX=-25.3585 CenterY=25 CenterZ=0 NormalX=0 NormalY=0 NormalZ=1 AngleXU=0 Radius=1.5
    g3: LineSegment [constr] StartX=-47.1325 StartY=25 StartZ=0 EndX=65.8699 EndY=25 EndZ=0
  constraints (9):
    c: PointOnObject(g0,g-2)
    c: PointOnObject(g1,g-2)
    c: Diameter(g0) = 3
    c: Diameter(g1) = 3
    c: Distance(g0,g-1) = 6
    c: DistanceY(g-1,g1) = 44
    c: Diameter(g2) = 3
    c: Symmetric(g1,g0,g3)
    c: PointOnObject(g2,g3)
FEATURE [PartDesign::Pocket] Pocket006
  BaseFeature = -> Mirrored
  Direction = (-1,0,0)
  Length = 38
  Length2 = 30
  Placement = pos=(0,0,0) rot=(1,0,0;1.5708rad)
  Profile = -> Sketch015
  ReferenceAxis = -> Sketch015 [N_Axis]
  Reversed = true
  Suppressed = false
  Type = 4
FEATURE [PartDesign::Body] Body004  label="T"
  AllowCompound = false
  Group = -> [Sketch011,Sketch012,Pad008,Pad007,Sketch013,Pocket005,Sketch014,Pad009,Mirrored,Sketch015,Pocket006]
  Origin = -> Origin005
  Tip = -> Pocket006
FEATURE [App::Link] Roulement  label="Roulement001"
  LinkPlacement = pos=(0,4.17233e-06,-35) rot=(0,0,1;0rad)
  LinkedObject = -> Body002
  Placement = pos=(0,4.17233e-06,-35) rot=(0,0,1;0rad)
FEATURE [App::Link] T  label="T001"
  LinkPlacement = pos=(0.13305,0.133042,88.1331) rot=(0,0,1;0rad)
  LinkedObject = -> Body004
  Placement = pos=(0.13305,0.133042,88.1331) rot=(0,0,1;0rad)
FEATURE [Sketcher::SketchObject] Sketch016
  ArcFitTolerance = 1e-06
  AttachmentSupport = -> [XY_Plane006]
  FullyConstrained = false
  MakeInternals = false
  MapMode = 5
  sketch-geometry (2):
    g0: Circle CenterX=0 CenterY=0 CenterZ=0 NormalX=0 NormalY=0 NormalZ=1 AngleXU=0 Radius=9.90136
    g1: Circle CenterX=0 CenterY=0 CenterZ=0 NormalX=0 NormalY=0 NormalZ=1 AngleXU=0 Radius=9.36508
  constraints (2):
    c: Coincident(g0,g-1)
    c: Coincident(g1,g0)
FEATURE [PartDesign::Pad] Pad010
  Direction = (0,0,1)
  Length = 70
  Length2 = 10
  Profile = -> Sketch016
  ReferenceAxis = -> Sketch016 [N_Axis]
  Suppressed = false
  Type = 0
FEATURE [PartDesign::Body] Body005  label="Axe simple"
  AllowCompound = false
  Group = -> [Sketch016,Pad010]
  Origin = -> Origin006
  Tip = -> Pad010
FEATURE [App::Link] Axe_simple  label="Axe simple001"
  LinkPlacement = pos=(0,1.78814e-06,-15) rot=(0,0,1;0rad)
  LinkedObject = -> Body005
  Placement = pos=(0,1.78814e-06,-15) rot=(0,0,1;0rad)
FEATURE [Assembly::AssemblyObject] Assembly
  Group = -> [Joints,Support_mur,GroundedJoint,Axe,Bouchon,Exploded_Views,Exploded_View,Move,Move001,Move002,Roulement,T,Axe_simple]
  Origin = -> Origin002
  Type = Assembly
note: 2 file-system paths scrubbed to <path> (originals preserved in the JSON sidecar)
